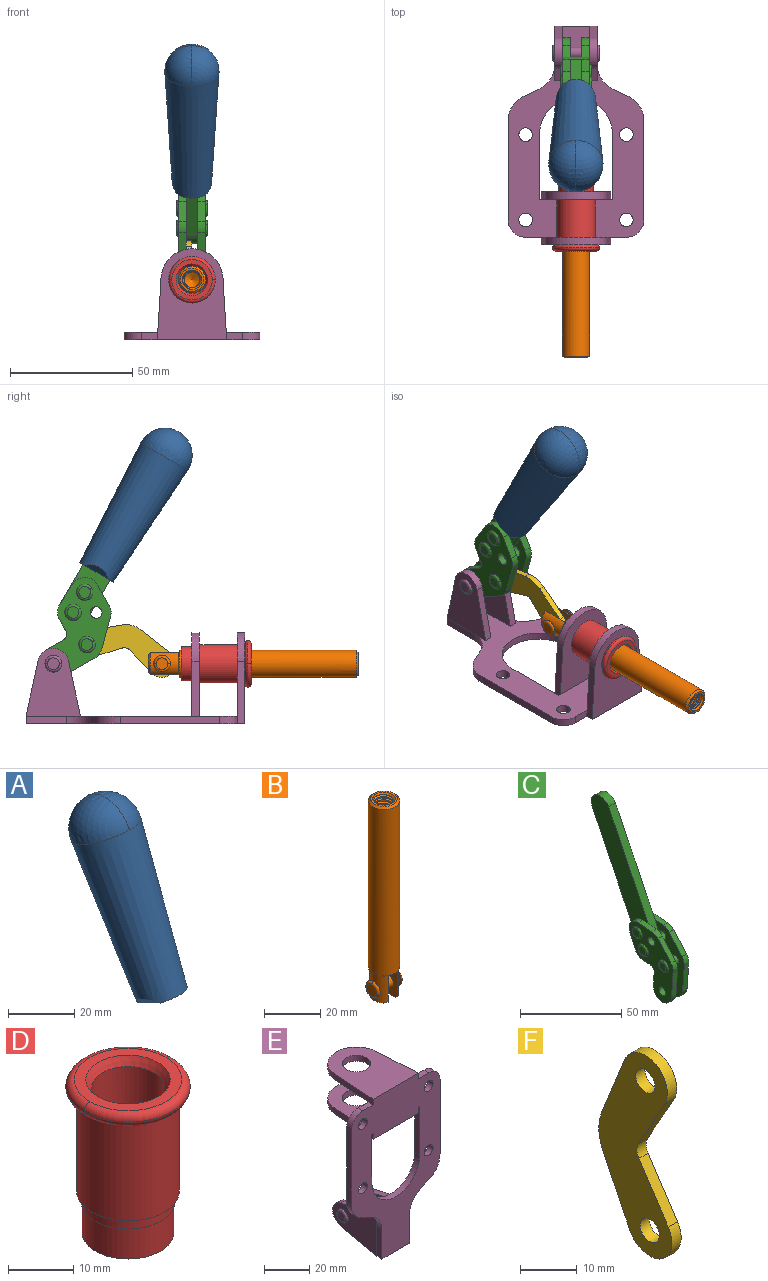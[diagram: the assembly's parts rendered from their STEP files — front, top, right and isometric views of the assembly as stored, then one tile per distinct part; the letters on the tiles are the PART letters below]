
ASSEMBLY  parts=6 mates=6
PART A: 11 faces, bbox 22.3x42.6x64.5 mm
  f0: sphere r=11.13mm, area 411.4mm2, adj f1,f8
  f1: cone r=11.11mm half-angle=3.3deg, axis (0,0.44,0.9), area 3251.8mm2, adj f0,f7,f8,f9,f10
  f2: cylinder r=6.16mm len=11.7mm, axis (1,0,0), area 89.5mm2, adj f3,f4,f5,f6
  f3: plane 60.23x36.75mm, normal (-1,0,0), area 763.6mm2, adj f2,f4,f6,f10
  f4: plane 51.37x25.05mm, normal (0,0.9,-0.44), area 264.2mm2, adj f2,f3,f5,f10
  f5: plane 60.23x36.75mm, normal (1,0,0), area 763.6mm2, adj f2,f4,f6,f10
  f6: plane 51.37x25.05mm, normal (0,-0.9,0.44), area 264.2mm2, adj f2,f3,f5,f10
  f7: plane 9.95x5.95mm, normal (0.71,-0.31,-0.64), area 25.8mm2, adj f1,f10
  f8: sphere r=11.13mm, area 411.4mm2, adj f0,f1
  f9: plane 9.95x5.95mm, normal (-0.71,-0.31,-0.64), area 25.8mm2, adj f1,f10
  f10: plane 14.27x11.38mm, normal (0,-0.44,-0.9), area 106.7mm2, adj f1,f3,f4,f5,f6,f7,f9
PART B: 48 faces, bbox 12.6x11.1x86.1 mm
  f0: torus R=2.41mm, axis (-1,0,0), area 15mm2, adj f30,f32,f34
  f1: torus R=2.41mm, axis (-1,0,0), area 15mm2, adj f29,f31,f33
  f2: cylinder r=5.54mm len=72.39mm, axis (0,0,1), area 2518.5mm2, adj f3,f4,f42,f43
  f3: cone r=5.54mm half-angle=45deg, axis (0,0,1), area 7.6mm2, adj f2,f5,f41
  f4: cone r=5.54mm half-angle=45deg, axis (0,0,-1), area 34.9mm2, adj f2,f39
  f5: cylinder r=5.08mm len=11.48mm, axis (0,0,1), area 108.3mm2, adj f3,f7,f8,f41
  f6: cylinder r=2.41mm len=4.83mm, axis (-1,0,0), area 71.2mm2, adj f40,f41
  f7: cylinder r=2.41mm len=4.83mm, axis (-1,0,0), area 7.6mm2, adj f5,f34
  f8: cone r=5.08mm half-angle=45deg, axis (0,0,1), area 10.6mm2, adj f5,f37,f41
  f9: cone r=3.98mm half-angle=45deg, axis (0,0,1), area 17.6mm2, adj f27,f39,f45,f46,f47
  f10: cylinder r=2.41mm len=4.83mm, axis (-1,0,0), area 7.6mm2, adj f33,f38
  f11: cylinder r=3.2mm len=6.4mm, axis (0,0,1), area 78.4mm2, adj f12,f28,f44,f45,f47
  f12: cylinder r=3.2mm len=6.4mm, axis (0,0,1), area 10.5mm2, adj f11,f13,f45,f47
  f13: cylinder r=3.2mm len=6.4mm, axis (0,0,1), area 10.5mm2, adj f12,f14,f45,f47
  f14: cylinder r=3.2mm len=6.4mm, axis (0,0,1), area 10.5mm2, adj f13,f15,f45,f47
  f15: cylinder r=3.2mm len=6.4mm, axis (0,0,1), area 10.5mm2, adj f14,f16,f45,f47
  f16: cylinder r=3.2mm len=6.4mm, axis (0,0,1), area 10.5mm2, adj f15,f17,f45,f47
  f17: cylinder r=3.2mm len=6.4mm, axis (0,0,1), area 10.5mm2, adj f16,f18,f45,f47
  f18: cylinder r=3.2mm len=6.4mm, axis (0,0,1), area 10.5mm2, adj f17,f19,f45,f47
  f19: cylinder r=3.2mm len=6.4mm, axis (0,0,1), area 10.5mm2, adj f18,f20,f45,f47
  f20: cylinder r=3.2mm len=6.4mm, axis (0,0,1), area 10.5mm2, adj f19,f21,f45,f47
  f21: cylinder r=3.2mm len=6.4mm, axis (0,0,1), area 10.5mm2, adj f20,f22,f45,f47
  f22: cylinder r=3.2mm len=6.4mm, axis (0,0,1), area 10.5mm2, adj f21,f23,f45,f47
  f23: cylinder r=3.2mm len=6.4mm, axis (0,0,1), area 10.5mm2, adj f22,f24,f45,f47
  f24: cylinder r=3.2mm len=6.4mm, axis (0,0,1), area 10.5mm2, adj f23,f25,f45,f47
  f25: cylinder r=3.2mm len=6.4mm, axis (0,0,1), area 10.5mm2, adj f24,f26,f45,f47
  f26: cylinder r=3.2mm len=6.4mm, axis (0,0,1), area 10.5mm2, adj f25,f27,f45,f47
  f27: cylinder r=3.2mm len=6.4mm, axis (0,0,1), area 7.4mm2, adj f9,f26,f45,f47
  f28: cone r=3.2mm half-angle=60deg, axis (0,0,1), area 37.2mm2, adj f11
  f29: plane 4.83x4.83mm, normal (-1,0,0), area 18.3mm2, adj f1,f31
  f30: plane 4.83x4.83mm, normal (1,0,0), area 18.3mm2, adj f0,f32
  f31: torus R=2.41mm, axis (-1,0,0), area 15mm2, adj f1,f29,f33
  f32: torus R=2.41mm, axis (-1,0,0), area 15mm2, adj f0,f30,f34
  f33: plane 6.83x6.83mm, normal (1,0,0), area 18.3mm2, adj f1,f10,f31
  f34: plane 6.83x6.83mm, normal (-1,0,0), area 18.3mm2, adj f0,f7,f32
  f35: cone r=5.08mm half-angle=45deg, axis (0,0,1), area 10.6mm2, adj f36,f38,f40
  f36: plane 7.25x1.97mm, normal (0,0,-1), area 10mm2, adj f35,f40
  f37: plane 7.25x1.97mm, normal (0,0,-1), area 10mm2, adj f8,f41
  f38: cylinder r=5.08mm len=11.48mm, axis (0,0,1), area 108.3mm2, adj f10,f35,f40,f42
  f39: plane 9.55x9.55mm, normal (0,0,1), area 22mm2, adj f4,f9
  f40: plane 12.76x10.09mm, normal (1,0,0), area 95.7mm2, adj f6,f35,f36,f38,f42,f43
  f41: plane 12.76x10.09mm, normal (-1,0,0), area 95.7mm2, adj f3,f5,f6,f8,f37,f43
  f42: cone r=5.54mm half-angle=45deg, axis (0,0,1), area 7.6mm2, adj f2,f38,f40
  f43: plane 11.07x4.7mm, normal (0,0,-1), area 50.4mm2, adj f2,f40,f41
  f44: plane 0.89x0.62mm, normal (-1,0,0), area 0.3mm2, adj f11,f45,f46,f47
  f45: bspline ~24.8x7.63mm, area 266.6mm2, adj f9,f11,f12,f13,f14,f15,f16,f17
  f46: bspline ~24.87x7.63mm, area 73.6mm2, adj f9,f44,f45,f47
  f47: bspline ~24.98x7.63mm, area 272.5mm2, adj f9,f11,f12,f13,f14,f15,f16,f17
PART C: 59 faces, bbox 12.9x60.2x99.6 mm
  f0: torus R=2.39mm, axis (-1,0,0), area 14.9mm2, adj f20,f43,f51
  f1: torus R=2.39mm, axis (-1,0,0), area 14.9mm2, adj f19,f42,f51
  f2: torus R=2.39mm, axis (-1,0,0), area 14.9mm2, adj f18,f35,f51
  f3: torus R=2.39mm, axis (-1,0,0), area 14.9mm2, adj f14,f17,f23
  f4: torus R=2.39mm, axis (-1,0,0), area 14.9mm2, adj f13,f16,f23
  f5: torus R=2.39mm, axis (-1,0,0), area 14.9mm2, adj f12,f15,f23
  f6: cylinder r=2.39mm len=4.78mm, axis (1,0,0), area 46.5mm2, adj f48,f50,f51
  f7: cylinder r=2.39mm len=4.78mm, axis (1,0,0), area 46.5mm2, adj f50,f51
  f8: cylinder r=6.35mm len=12.68mm, axis (1,0,0), area 61.8mm2, adj f38,f39,f50,f51
  f9: cylinder r=2.39mm len=4.78mm, axis (-1,0,0), area 70.5mm2, adj f46,f50
  f10: cylinder r=2.39mm len=4.78mm, axis (-1,0,0), area 46.5mm2, adj f23,f45,f46
  f11: cylinder r=2.39mm len=4.78mm, axis (-1,0,0), area 46.5mm2, adj f23,f46
  f12: plane 4.78x4.78mm, normal (1,0,0), area 17.9mm2, adj f5,f15
  f13: plane 4.78x4.78mm, normal (1,0,0), area 17.9mm2, adj f4,f16
  f14: plane 4.78x4.78mm, normal (1,0,0), area 17.9mm2, adj f3,f17
  f15: torus R=2.39mm, axis (-1,0,0), area 14.9mm2, adj f5,f12,f23
  f16: torus R=2.39mm, axis (-1,0,0), area 14.9mm2, adj f4,f13,f23
  f17: torus R=2.39mm, axis (-1,0,0), area 14.9mm2, adj f3,f14,f23
  f18: plane 4.78x4.78mm, normal (-1,0,0), area 17.9mm2, adj f2,f35
  f19: plane 4.78x4.78mm, normal (-1,0,0), area 17.9mm2, adj f1,f42
  f20: plane 4.78x4.78mm, normal (-1,0,0), area 17.9mm2, adj f0,f43
  f21: plane 2.26x0.2mm, normal (1,0,0), area 0.2mm2, adj f31,f44
  f22: plane 2.26x0.2mm, normal (-1,0,0), area 0.2mm2, adj f41,f44
  f23: plane 39.37x30.77mm, normal (1,0,0), area 565.5mm2, adj f3,f4,f5,f10,f11,f15,f16,f17
  f24: cylinder r=6.1mm len=4.15mm, axis (-1,0,0), area 14.7mm2, adj f23,f25,f32,f46
  f25: plane 10.25x9.01mm, normal (0,-0.75,0.66), area 42.3mm2, adj f23,f24,f26,f46
  f26: cylinder r=6.35mm len=4.64mm, axis (-1,0,0), area 15.6mm2, adj f23,f25,f27,f46
  f27: plane 15.84x3.1mm, normal (0,-1,-0.07), area 49.2mm2, adj f23,f26,f28,f46
  f28: cylinder r=6.35mm len=12.68mm, axis (-1,0,0), area 61.8mm2, adj f23,f27,f29,f46
  f29: plane 8.11x3.1mm, normal (0,1,0.07), area 25.2mm2, adj f23,f28,f30,f46
  f30: cylinder r=3.05mm len=3.25mm, axis (-1,0,0), area 14.8mm2, adj f23,f29,f31,f46
  f31: plane 5.99x3.1mm, normal (0,0.07,-1), area 18.6mm2, adj f21,f23,f30,f44,f46
  f32: plane 9.5x3.1mm, normal (0,-0.07,1), area 29.5mm2, adj f23,f24,f33,f46,f47
  f33: cylinder r=6.1mm len=8.63mm, axis (-1,0,0), area 39.1mm2, adj f23,f32,f34,f47
  f34: plane 8.65x3.96mm, normal (0,0.91,-0.42), area 29.5mm2, adj f23,f33,f44,f47
  f35: torus R=2.39mm, axis (-1,0,0), area 14.9mm2, adj f2,f18,f51
  f36: plane 10.25x9.01mm, normal (0,-0.75,0.66), area 42.3mm2, adj f37,f49,f50,f51
  f37: cylinder r=6.35mm len=4.64mm, axis (1,0,0), area 15.6mm2, adj f36,f38,f50,f51
  f38: plane 15.84x3.1mm, normal (0,-1,-0.07), area 49.2mm2, adj f8,f37,f50,f51
  f39: plane 8.11x3.1mm, normal (0,1,0.07), area 25.2mm2, adj f8,f40,f50,f51
  f40: cylinder r=3.05mm len=3.25mm, axis (1,0,0), area 14.8mm2, adj f39,f41,f50,f51
  f41: plane 5.99x3.1mm, normal (0,0.07,-1), area 18.6mm2, adj f22,f40,f44,f50,f51
  f42: torus R=2.39mm, axis (-1,0,0), area 14.9mm2, adj f1,f19,f51
  f43: torus R=2.39mm, axis (-1,0,0), area 14.9mm2, adj f0,f20,f51
  f44: cylinder r=6.35mm len=12.12mm, axis (-1,0,0), area 128.9mm2, adj f21,f22,f23,f31,f34,f41,f46,f47
  f45: plane 2.65x1.35mm, normal (1,0,0), area 1mm2, adj f10,f55
  f46: plane 39.08x20.42mm, normal (-1,0,0), area 412.5mm2, adj f9,f10,f11,f24,f25,f26,f27,f28
  f47: plane 77.62x39.82mm, normal (1,0,0), area 850mm2, adj f32,f33,f34,f44,f53,f54,f55
  f48: plane 2.65x1.35mm, normal (-1,0,0), area 1mm2, adj f6,f55
  f49: cylinder r=6.1mm len=4.15mm, axis (1,0,0), area 14.7mm2, adj f36,f50,f51,f56
  f50: plane 39.08x20.42mm, normal (1,0,0), area 412.5mm2, adj f6,f7,f8,f9,f36,f37,f38,f39
  f51: plane 39.37x30.77mm, normal (-1,0,0), area 565.5mm2, adj f0,f1,f2,f6,f7,f8,f35,f36
  f52: plane 8.65x3.96mm, normal (0,0.91,-0.42), area 29.5mm2, adj f44,f51,f57,f58
  f53: plane 68.49x33.4mm, normal (0,0.9,-0.44), area 358.1mm2, adj f44,f47,f54,f58
  f54: cylinder r=6.35mm len=12.06mm, axis (1,0,0), area 93.7mm2, adj f47,f53,f55,f58
  f55: plane 68.49x33.4mm, normal (0,-0.9,0.44), area 358.1mm2, adj f44,f45,f46,f47,f48,f50,f54,f58
  f56: plane 9.5x3.1mm, normal (0,-0.07,1), area 29.5mm2, adj f49,f50,f51,f57,f58
  f57: cylinder r=6.1mm len=8.63mm, axis (1,0,0), area 39.1mm2, adj f51,f52,f56,f58
  f58: plane 77.62x39.82mm, normal (-1,0,0), area 850mm2, adj f44,f52,f53,f54,f55,f56,f57
PART D: 15 faces, bbox 20.6x20.6x28.7 mm
  f0: torus R=8.26mm, axis (0,0,1), area 56.8mm2, adj f1,f10,f12
  f1: torus R=8.26mm, axis (0,0,1), area 56.8mm2, adj f0,f6,f13
  f2: cylinder r=5.59mm len=25.91mm, axis (0,0,1), area 909.6mm2, adj f3,f4
  f3: cone r=6.86mm half-angle=45deg, axis (0,0,-1), area 70.2mm2, adj f2,f14
  f4: cone r=6.47mm half-angle=30deg, axis (0,0,1), area 66.7mm2, adj f2,f13
  f5: cylinder r=7.04mm len=14.07mm, axis (0,0,1), area 252.6mm2, adj f11,f14
  f6: torus R=8.26mm, axis (0,0,1), area 56.8mm2, adj f1,f12,f13
  f7: cylinder r=7.16mm len=14.33mm, axis (0,0,1), area 91.5mm2, adj f9,f11
  f8: cylinder r=7.86mm len=18.42mm, axis (0,0,1), area 909.6mm2, adj f9,f10
  f9: plane 15.72x15.72mm, normal (0,0,-1), area 33mm2, adj f7,f8
  f10: plane 16.51x16.51mm, normal (0,0,-1), area 19.9mm2, adj f0,f8,f12
  f11: plane 14.33x14.33mm, normal (0,0,-1), area 5.7mm2, adj f5,f7
  f12: torus R=8.26mm, axis (0,0,1), area 56.8mm2, adj f0,f6,f10
  f13: plane 16.51x16.51mm, normal (0,0,1), area 82.7mm2, adj f1,f4,f6
  f14: plane 14.07x14.07mm, normal (0,0,-1), area 7.8mm2, adj f3,f5
PART E: 55 faces, bbox 55.7x37.4x89.8 mm
  f0: torus R=2.41mm, axis (-1,0,0), area 15mm2, adj f11,f15,f25
  f1: torus R=2.41mm, axis (-1,0,0), area 15mm2, adj f10,f12,f22
  f2: cylinder r=2.78mm len=5.56mm, axis (0,-1,0), area 54.2mm2, adj f30,f54
  f3: cylinder r=14.99mm len=29.97mm, axis (0,-1,0), area 145.9mm2, adj f30,f49,f53,f54
  f4: cylinder r=2.78mm len=5.56mm, axis (0,-1,0), area 54.2mm2, adj f30,f54
  f5: cylinder r=2.78mm len=5.56mm, axis (0,-1,0), area 54.2mm2, adj f30,f54
  f6: cylinder r=2.78mm len=5.56mm, axis (0,-1,0), area 54.2mm2, adj f30,f54
  f7: cylinder r=6.35mm len=12.7mm, axis (0,0,1), area 123.6mm2, adj f27,f51
  f8: cylinder r=6.35mm len=12.7mm, axis (0,0,-1), area 124.7mm2, adj f21,f35
  f9: cylinder r=2.41mm len=11.18mm, axis (-1,0,0), area 169.4mm2, adj f16,f19
  f10: plane 4.83x4.83mm, normal (1,0,0), area 18.3mm2, adj f1,f12
  f11: plane 4.83x4.83mm, normal (-1,0,0), area 18.3mm2, adj f0,f15
  f12: torus R=2.41mm, axis (-1,0,0), area 15mm2, adj f1,f10,f22
  f13: cylinder r=6.35mm len=12.41mm, axis (1,0,0), area 53.4mm2, adj f18,f19,f22,f23
  f14: cylinder r=6.35mm len=12.41mm, axis (-1,0,0), area 53.4mm2, adj f16,f17,f24,f25
  f15: torus R=2.41mm, axis (-1,0,0), area 15mm2, adj f0,f11,f25
  f16: plane 27.86x22.35mm, normal (1,0,0), area 425.4mm2, adj f9,f14,f17,f24,f30
  f17: plane 22.86x4.97mm, normal (0,0.21,0.98), area 72.5mm2, adj f14,f16,f25,f30
  f18: plane 22.86x4.97mm, normal (0,0.21,0.98), area 72.5mm2, adj f13,f19,f22,f30
  f19: plane 27.86x22.35mm, normal (-1,0,0), area 425.4mm2, adj f9,f13,f18,f23,f30
  f20: cylinder r=12.7mm len=25.35mm, axis (0,0,-1), area 119.8mm2, adj f21,f34,f35,f36
  f21: plane 34.21x28.07mm, normal (0,0,-1), area 702.4mm2, adj f8,f20,f30,f34,f36
  f22: plane 27.96x22.45mm, normal (1,0,0), area 407.2mm2, adj f1,f12,f13,f18,f23,f30,f42,f43
  f23: plane 22.86x4.97mm, normal (0,0.21,-0.98), area 72.5mm2, adj f13,f19,f22,f44
  f24: plane 22.86x4.97mm, normal (0,0.21,-0.98), area 72.5mm2, adj f14,f16,f25,f44
  f25: plane 27.86x22.35mm, normal (-1,0,0), area 407.1mm2, adj f0,f14,f15,f17,f24,f30,f45,f46
  f26: plane 3.1x0.95mm, normal (0,0,-1), area 2.7mm2, adj f30,f49,f50,f54
  f27: plane 34.21x28.07mm, normal (0,0,1), area 702.4mm2, adj f7,f28,f30,f50,f52
  f28: cylinder r=12.7mm len=25.35mm, axis (0,0,1), area 118.8mm2, adj f27,f50,f51,f52
  f29: plane 3.1x0.95mm, normal (0,0,-1), area 2.7mm2, adj f30,f52,f53,f54
  f30: plane 86.54x55.63mm, normal (0,1,0), area 2362.9mm2, adj f2,f3,f4,f5,f6,f16,f17,f18
  f31: plane 40.56x3.1mm, normal (-1,0,0), area 125.7mm2, adj f30,f32,f48,f54
  f32: cylinder r=7.11mm len=7.11mm, axis (0,-1,0), area 34.6mm2, adj f30,f31,f33,f54
  f33: plane 6.67x3.1mm, normal (0,0,1), area 20.4mm2, adj f30,f32,f34,f54
  f34: plane 25.39x3.13mm, normal (-1,0.06,0), area 79.5mm2, adj f20,f21,f33,f35,f54
  f35: plane 37.31x28.45mm, normal (0,0,1), area 789.9mm2, adj f8,f20,f34,f36,f54
  f36: plane 25.39x3.13mm, normal (1,0.06,0), area 79.5mm2, adj f20,f21,f35,f37,f54
  f37: plane 6.67x3.1mm, normal (0,0,1), area 20.4mm2, adj f30,f36,f38,f54
  f38: cylinder r=7.11mm len=7.11mm, axis (0,-1,0), area 34.6mm2, adj f30,f37,f39,f54
  f39: plane 40.56x3.1mm, normal (1,0,0), area 125.7mm2, adj f30,f38,f40,f54
  f40: cylinder r=11.18mm len=10.16mm, axis (0,-1,0), area 39.5mm2, adj f30,f39,f41,f54
  f41: plane 6.09x3.1mm, normal (0.42,0,-0.91), area 20.8mm2, adj f30,f40,f42,f54
  f42: cylinder r=11.18mm len=9.41mm, axis (0,-1,0), area 37.2mm2, adj f22,f30,f41,f43,f54
  f43: plane 16.5x3.1mm, normal (1,0,0), area 51.1mm2, adj f22,f42,f44,f54
  f44: plane 17.37x3.1mm, normal (0,0,-1), area 53.8mm2, adj f23,f24,f30,f43,f45,f54
  f45: plane 16.5x3.1mm, normal (-1,0,0), area 51.1mm2, adj f25,f44,f46,f54
  f46: cylinder r=11.18mm len=9.41mm, axis (0,-1,0), area 37.2mm2, adj f25,f30,f45,f47,f54
  f47: plane 6.09x3.1mm, normal (-0.42,0,-0.91), area 20.8mm2, adj f30,f46,f48,f54
  f48: cylinder r=11.18mm len=10.16mm, axis (0,-1,0), area 39.5mm2, adj f30,f31,f47,f54
  f49: plane 26.54x3.1mm, normal (-1,0,0), area 82.3mm2, adj f3,f26,f30,f54
  f50: plane 25.39x3.1mm, normal (1,0.06,0), area 78.8mm2, adj f26,f27,f28,f51,f54
  f51: plane 37.31x28.45mm, normal (0,0,-1), area 789.9mm2, adj f7,f28,f50,f52,f54
  f52: plane 25.39x3.1mm, normal (-1,0.06,0), area 78.8mm2, adj f27,f28,f29,f51,f54
  f53: plane 26.54x3.1mm, normal (1,0,0), area 82.3mm2, adj f3,f29,f30,f54
  f54: plane 89.66x55.63mm, normal (0,-1,0), area 2678.5mm2, adj f2,f3,f4,f5,f6,f26,f29,f31
PART F: 12 faces, bbox 2.3x18.2x42.8 mm
  f0: cylinder r=2.4mm len=4.8mm, axis (1,0,0), area 34.9mm2, adj f4,f11
  f1: cylinder r=10.41mm len=8.47mm, axis (1,0,0), area 20.2mm2, adj f4,f9,f10,f11
  f2: cylinder r=3.05mm len=3.16mm, axis (1,0,0), area 7.7mm2, adj f4,f6,f7,f11
  f3: cylinder r=2.4mm len=4.8mm, axis (1,0,0), area 34.9mm2, adj f4,f11
  f4: plane 42.81x18.23mm, normal (-1,0,0), area 414.1mm2, adj f0,f1,f2,f3,f5,f6,f7,f8
  f5: cylinder r=5.54mm len=10.67mm, axis (1,0,0), area 41.8mm2, adj f4,f6,f10,f11
  f6: plane 11.66x6.53mm, normal (0,-0.87,-0.49), area 30.9mm2, adj f2,f4,f5,f11
  f7: plane 11.17x7.33mm, normal (0,-0.84,0.55), area 30.9mm2, adj f2,f4,f8,f11
  f8: cylinder r=5.54mm len=10.51mm, axis (1,0,0), area 41.8mm2, adj f4,f7,f9,f11
  f9: plane 13.67x6.67mm, normal (0,0.9,-0.44), area 35.1mm2, adj f1,f4,f8,f11
  f10: plane 14.1x5.7mm, normal (0,0.93,0.37), area 35.1mm2, adj f1,f4,f5,f11
  f11: plane 42.81x18.23mm, normal (1,0,0), area 414.1mm2, adj f0,f1,f2,f3,f5,f6,f7,f8
PLACE A rot(axis=(1,0,0),56.3deg) t=(-0.04,0.88,21.91)mm
PLACE B rot(axis=(1,0,0),90deg) t=(0,12.15,0)mm
PLACE C rot(axis=(1,0,0),56.3deg) t=(0,0.88,21.91)mm
PLACE D rot(axis=(1,0,0),90deg) t=(0,9.14,0)mm
PLACE E rot(axis=(1,0,0),90deg) t=(0,9.14,0)mm fixed
PLACE F rot(axis=(1,0,0),106.3deg) t=(-1.16,18.44,5.34)mm
MATE revolute C.f7 <-> E.f0  axis (-1,0,0) through (0,41.23,24.61)mm
MATE fastened D.f2 <-> E.f7  axis (0,-1,0) through (0,-37.25,24.61)mm
MATE fastened A.f2 <-> C.f54  axis (1,0,0) through (-2.35,-5.34,111.4)mm
MATE revolute F.f5 <-> B.f6  axis (-1,0,0) through (0,-3.33,24.61)mm
MATE revolute F.f3 <-> C.f4  axis (-1,0,0) through (0,27.44,32.47)mm
MATE slider E.f7 <-> B.f2  axis (0,-1,0) through (0,-37.25,24.61)mm
